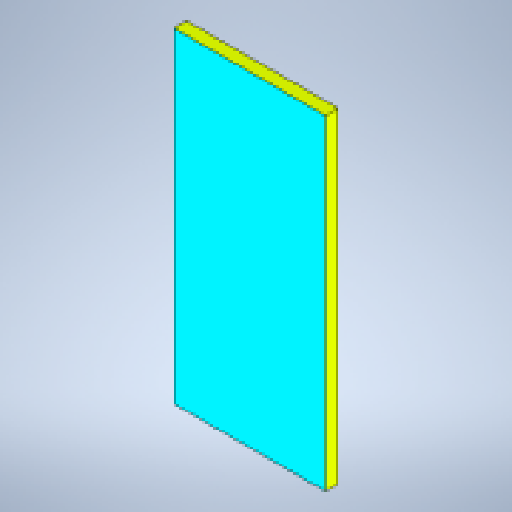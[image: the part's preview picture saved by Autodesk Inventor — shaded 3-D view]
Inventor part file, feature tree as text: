
AUTODESK INVENTOR PART (.ipt)
format: ipt  version: 2025.3 (Build 293356000, 356)  size: 126,464 bytes
history: native  units: mm
features: extrude x1, chamfer x1
ambient origin geometry x8: Origin, YZ Plane, XZ Plane, XY Plane, X Axis, Y Axis, Z Axis, Center Point
bodies: Solid1 (feature_tree)
feature tree (2):
  extrude  "Extrusion1"  Depth=1200.0mm
  chamfer  "Chamfer1"  Distance=2570.0mm
